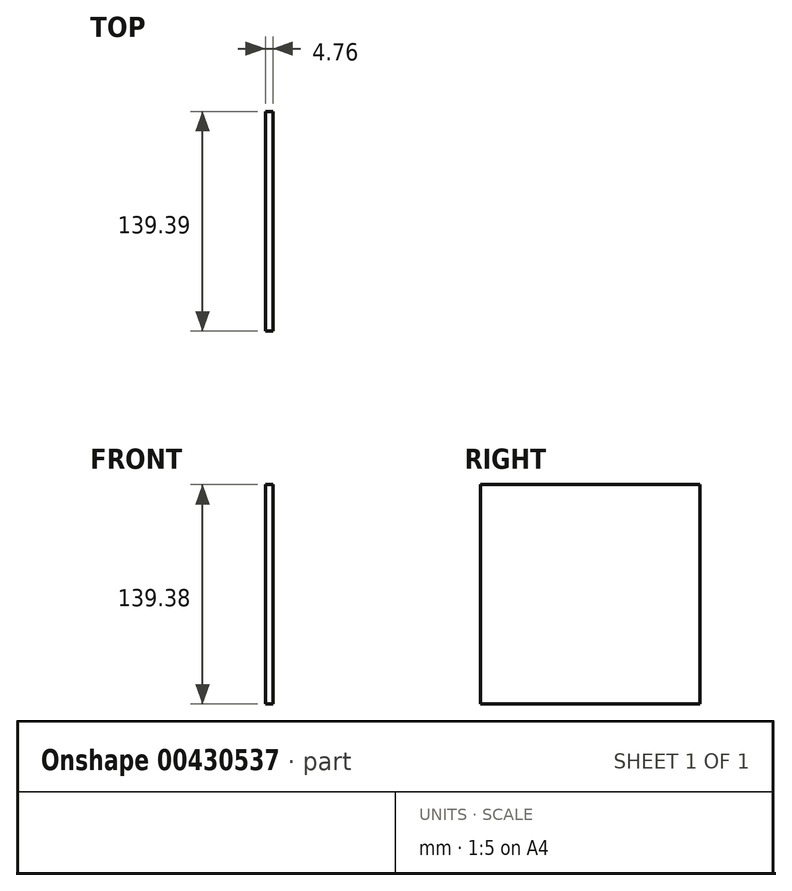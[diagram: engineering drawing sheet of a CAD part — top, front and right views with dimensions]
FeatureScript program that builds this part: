
annotation { "Feature Type Name" : "Feature", "Feature Type Description" : "" }
export const myFeature = defineFeature(function(context is Context, id is Id, definition is map)
    precondition{}
    {
        {
            var Q0;
            Q0=qCreatedBy(makeId("Right.planeOp"),FACE);
            var sketch = newSketch(context, id + "F0", { "sketchPlane" : qUnion([Q0])});
            skLineSegment(sketch, "E0.bottom", {"start": v(-57.69, 76.63) * mm, "end": v(81.7, 76.63) * mm});
            skLineSegment(sketch, "E0.top", {"start": v(-57.69, -62.75) * mm, "end": v(81.7, -62.75) * mm});
            skLineSegment(sketch, "E0.left", {"start": v(-57.69, 76.63) * mm, "end": v(-57.69, -62.75) * mm});
            skLineSegment(sketch, "E0.right", {"start": v(81.7, 76.63) * mm, "end": v(81.7, -62.75) * mm});
            skSolve(sketch);
        }
        {
            var Q0;
            Q0=makeQuery(id+"F0.imprint","IMPRINT",FACE,{"disambiguationData":[TD([[makeQuery(id+"F0.imprint","IMPRINT",EDGE,{"derivedFrom":sQuery(id+"F0.wireOp",EDGE,"E0.bottom")}),-1.0]])]});
            extrude(context, id + "F1", {"entities" : qUnion([Q0]), "depth" : 4.76 * mm});
        }
    });
